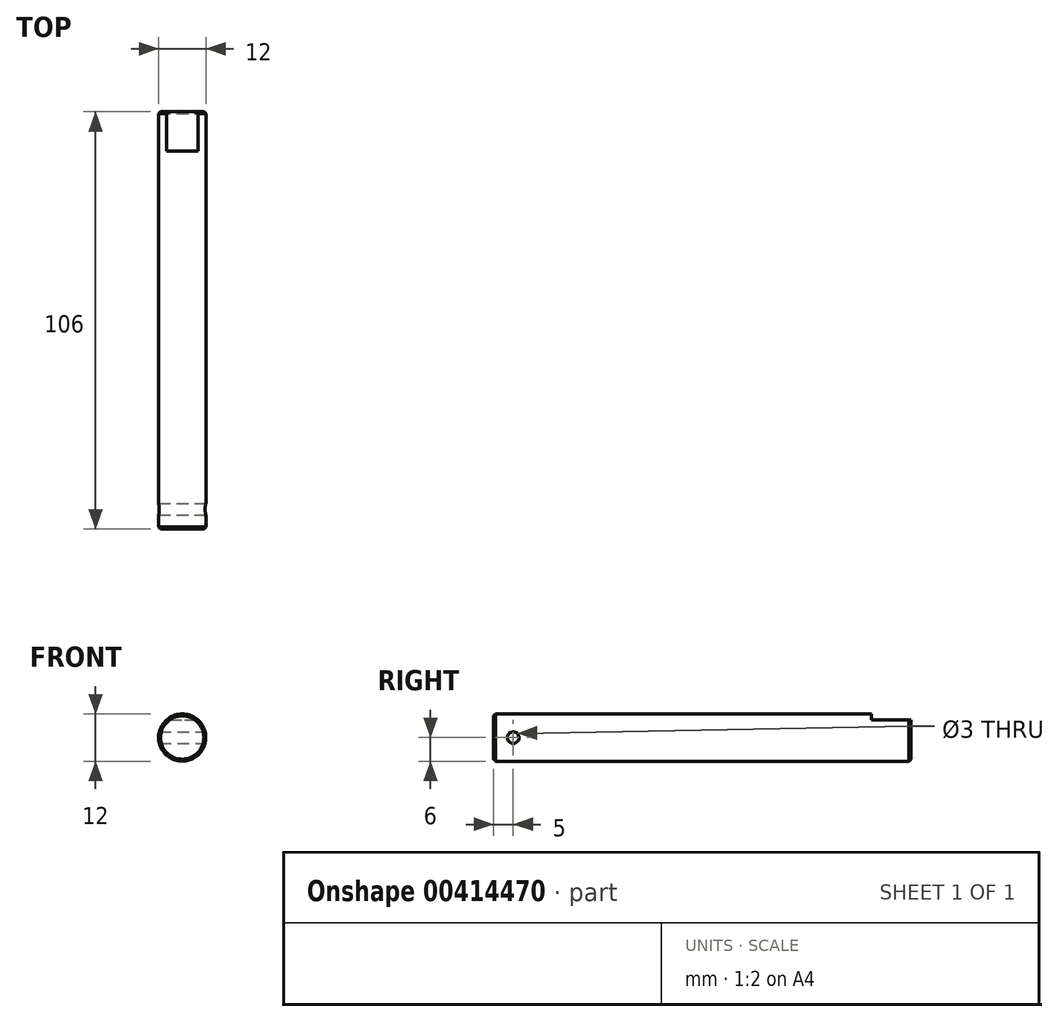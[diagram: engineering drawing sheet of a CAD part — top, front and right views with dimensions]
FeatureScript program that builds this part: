
annotation { "Feature Type Name" : "Feature", "Feature Type Description" : "" }
export const myFeature = defineFeature(function(context is Context, id is Id, definition is map)
    precondition{}
    {
        {
            var Q0;
            Q0=qCreatedBy(makeId("Front.planeOp"),FACE);
            var sketch = newSketch(context, id + "F0", { "sketchPlane" : qUnion([Q0])});
            skCircle(sketch, "E0", {"center": v(0, 0) * mm, "radius": 6 * mm});
            skSolve(sketch);
        }
        {
            var Q0;
            Q0=makeQuery(id+"F0.imprint","IMPRINT",FACE,{"disambiguationData":[TD([[makeQuery(id+"F0.imprint","IMPRINT",EDGE,{"derivedFrom":sQuery(id+"F0.wireOp",EDGE,"E0")}),1.0]])]});
            extrude(context, id + "F1", {"entities" : qUnion([Q0]), "depth" : 106 * mm});
        }
        {
            var Q0;
            Q0=makeQuery(id+"F1.opExtrude","CAP_EDGE",EDGE,{"disambiguationData":[OSD([sQuery(id+"F0.wireOp",EDGE,"E0")])],"isStart":false});
            var Q1;
            Q1=makeQuery(id+"F1.opExtrude","CAP_EDGE",EDGE,{"disambiguationData":[OSD([sQuery(id+"F0.wireOp",EDGE,"E0")])],"isStart":true});
            chamfer(context, id + "F2", {"entities" : qUnion([Q0, Q1]), "width" : .5 * mm, "tangentPropagation" : true});
        }
        {
            var Q0;
            Q0=qCreatedBy(makeId("Front.planeOp"),FACE);
            var sketch = newSketch(context, id + "F3", { "sketchPlane" : qUnion([Q0])});
            skLineSegment(sketch, "E1.bottom", {"start": v(-10, 9.5) * mm, "end": v(10, 9.5) * mm});
            skLineSegment(sketch, "E1.top", {"start": v(-10, 4.5) * mm, "end": v(10, 4.5) * mm});
            skLineSegment(sketch, "E1.left", {"start": v(-10, 9.5) * mm, "end": v(-10, 4.5) * mm});
            skLineSegment(sketch, "E1.right", {"start": v(10, 9.5) * mm, "end": v(10, 4.5) * mm});
            skSolve(sketch);
        }
        {
            var Q0;
            Q0=makeQuery(id+"F3.imprint","IMPRINT",FACE,{"disambiguationData":[TD([[makeQuery(id+"F3.imprint","IMPRINT",EDGE,{"derivedFrom":sQuery(id+"F3.wireOp",EDGE,"E1.bottom")}),-1.0]])]});
            extrude(context, id + "F4", {"entities" : qUnion([Q0]), "operationType" : NewBodyOperationType.REMOVE, "depth" : 10 * mm});
        }
        {
            var Q0;
            Q0=qCreatedBy(makeId("Right.planeOp"),FACE);
            var sketch = newSketch(context, id + "F5", { "sketchPlane" : qUnion([Q0])});
            skCircle(sketch, "E2", {"center": v(-101, 0) * mm, "radius": 1.5 * mm});
            skSolve(sketch);
        }
        {
            var Q0;
            Q0=makeQuery(id+"F5.imprint","IMPRINT",FACE,{"disambiguationData":[TD([[makeQuery(id+"F5.imprint","IMPRINT",EDGE,{"derivedFrom":sQuery(id+"F5.wireOp",EDGE,"E2")}),1.0]])]});
            extrude(context, id + "F6", {"entities" : qUnion([Q0]), "operationType" : NewBodyOperationType.REMOVE, "endBound" : BoundingType.SYMMETRIC, "oppositeDirection" : true, "depth" : 25 * mm});
        }
    });
